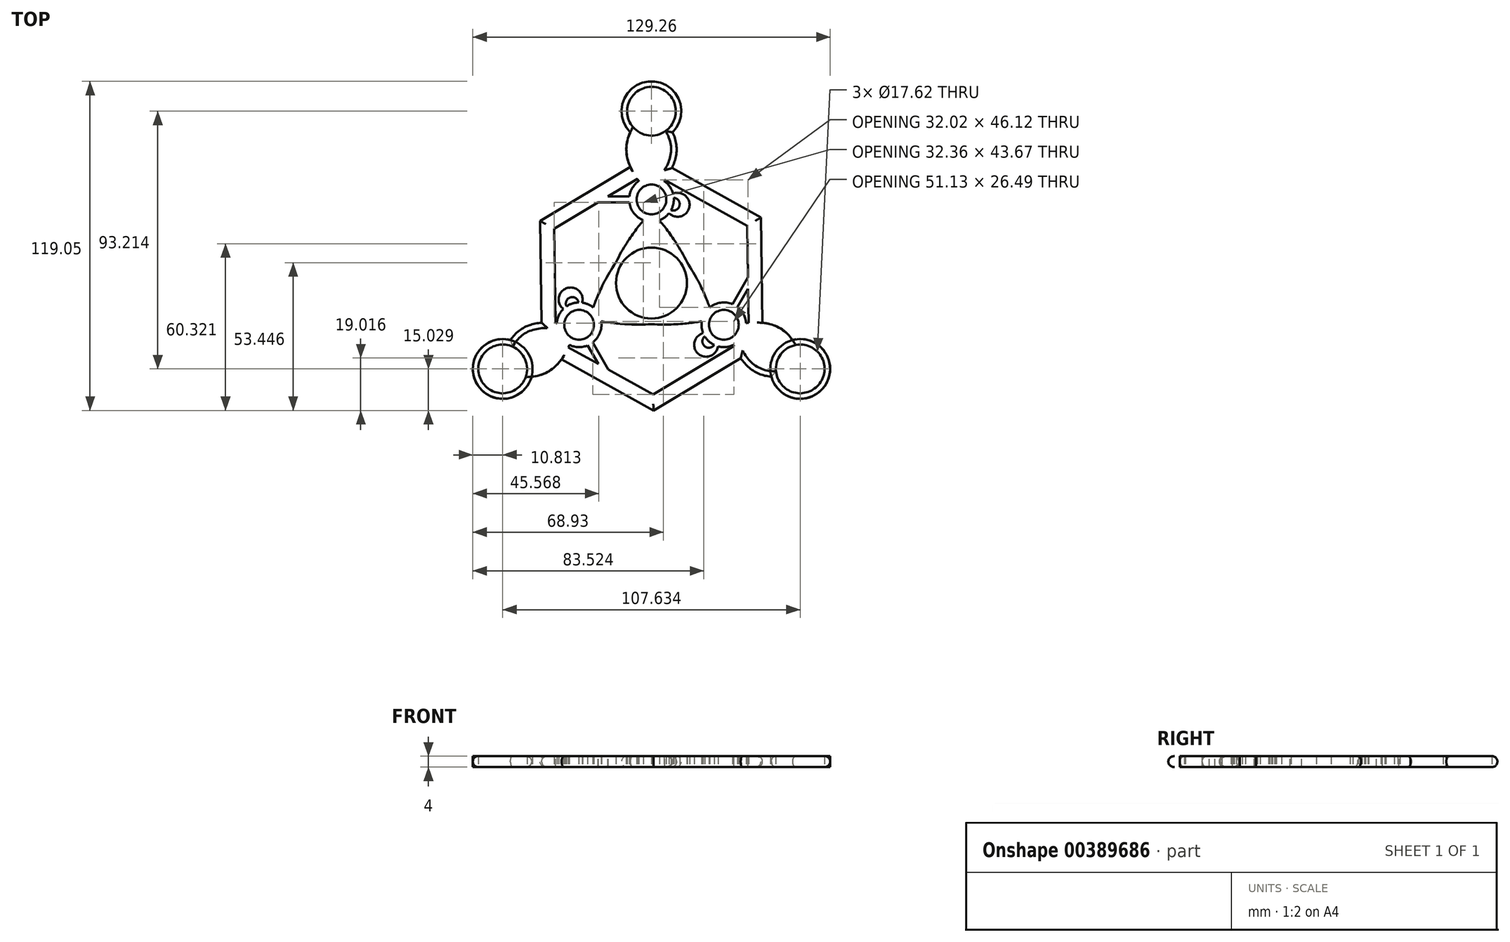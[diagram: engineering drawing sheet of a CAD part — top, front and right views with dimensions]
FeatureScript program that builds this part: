
annotation { "Feature Type Name" : "Feature", "Feature Type Description" : "" }
export const myFeature = defineFeature(function(context is Context, id is Id, definition is map)
    precondition{}
    {
        {
            var Q0;
            Q0=qCreatedBy(makeId("Top.planeOp"),FACE);
            var sketch = newSketch(context, id + "F0", { "sketchPlane" : qUnion([Q0])});
            skCircle(sketch, "E0", {"center": v(0, 0) * mm, "radius": 14.84 * mm});
            skCircle(sketch, "E1", {"center": v(0, 62.14) * mm, "radius": 10.8 * mm});
            skFitSpline(sketch, "E2", {"points": [v(-13.39, 6.4) * mm, v(0, 30.23) * mm, v(-7.64, 54.5) * mm], "startDerivative": vector(48.16, 100) * mm, "endDerivative": vector(32.63, 68.5) * mm});
            skFitSpline(sketch, "E3.MirrorCS", {"points": [v(13.39, 6.4) * mm, v(0, 30.23) * mm, v(7.64, 54.5) * mm], "startDerivative": vector(-48.16, 100) * mm, "endDerivative": vector(-32.63, 68.5) * mm});
            skCircle(sketch, "E4", {"center": v(0, 30.23) * mm, "radius": 5.38 * mm});
            skArc(sketch, "E5.0", {"start": v(-4.57, 36.9) * mm, "mid": v(-6.89, 34.45) * mm, "end": v(-8.01, 31.27) * mm});
            skFitSpline(sketch, "E6.trimOffspring", {"points": [v(-13.39, 6.4) * mm, v(0, 30.23) * mm, v(-7.64, 54.5) * mm], "startDerivative": vector(48.16, 100) * mm, "endDerivative": vector(32.63, 68.5) * mm});
            skLineSegment(sketch, "E7.trimOffspring", {"start": v(0, 30.23) * mm, "end": v(0, 30.23) * mm});
            skArc(sketch, "E8.trimOffspring", {"start": v(2.88, 22.68) * mm, "mid": v(6.82, 25.9) * mm, "end": v(8.06, 30.83) * mm});
            skCircle(sketch, "E9.1.0", {"center": v(-53.82, -31.07) * mm, "radius": 10.8 * mm});
            skCircle(sketch, "E9.2.0", {"center": v(53.82, -31.07) * mm, "radius": 10.8 * mm});
            skCircle(sketch, "E10.0", {"center": v(0, 0) * mm, "radius": 12.84 * mm});
            skCircle(sketch, "E11.0", {"center": v(0, 62.14) * mm, "radius": 8.8 * mm});
            skLineSegment(sketch, "E12.bottom", {"start": v(-20.22, 31.3) * mm, "end": v(-8.01, 31.3) * mm});
            skLineSegment(sketch, "E12.top", {"start": v(-20.22, 29.18) * mm, "end": v(-8.01, 29.18) * mm});
            skLineSegment(sketch, "E12.left", {"start": v(-20.22, 31.3) * mm, "end": v(-20.22, 29.18) * mm});
            skLineSegment(sketch, "E12.right", {"start": v(-8.01, 31.3) * mm, "end": v(-8.01, 31.27) * mm});
            skArc(sketch, "E13.trimOffspring", {"start": v(-8.01, 29.18) * mm, "mid": v(-6.34, 25.22) * mm, "end": v(-2.88, 22.68) * mm});
            skArc(sketch, "E14", {"start": v(7.08, 26.34) * mm, "mid": v(10.17, 28.03) * mm, "end": v(8.06, 30.83) * mm});
            skArc(sketch, "E15", {"start": v(5.35, 29.7) * mm, "mid": v(5.2, 29.16) * mm, "end": v(5.13, 28.62) * mm});
            skArc(sketch, "E16.trimOffspring", {"start": v(7.8, 32.3) * mm, "mid": v(6.6, 34.89) * mm, "end": v(4.57, 36.9) * mm});
            skArc(sketch, "E17.trimOffspring", {"start": v(6.37, 25.26) * mm, "mid": v(13.7, 27.43) * mm, "end": v(7.8, 32.3) * mm});
            skSolve(sketch);
        }
        {
            var Q0;
            Q0=qSketchRegion(id+"F0",true);
            extrude(context, id + "F1", {"entities" : qUnion([Q0]), "depth" : 4 * mm});
        }
        {
            var Q0;
            Q0=makeQuery(id+"F1.opExtrude","SWEPT_BODY",BODY,{"disambiguationData":[OSD([sQuery(id+"F0.wireOp",EDGE,"E0"),sQuery(id+"F0.wireOp",EDGE,"E1"),sQuery(id+"F0.wireOp",EDGE,"E2"),sQuery(id+"F0.wireOp",EDGE,"E3.MirrorCS"),sQuery(id+"F0.wireOp",EDGE,"E4"),sQuery(id+"F0.wireOp",EDGE,"E5.0"),sQuery(id+"F0.wireOp",EDGE,"E3.MirrorCS"),sQuery(id+"F0.wireOp",EDGE,"E6.trimOffspring"),sQuery(id+"F0.wireOp",EDGE,"E8.trimOffspring"),sQuery(id+"F0.wireOp",EDGE,"E10.0"),sQuery(id+"F0.wireOp",EDGE,"E11.0")])]});
            var Q1;
            Q1=makeQuery(id+"F1.opExtrude","CAP_EDGE",EDGE,{"disambiguationData":[OSD([sQuery(id+"F0.wireOp",EDGE,"E10.0")])],"isStart":false});
            circularPattern(context, id + "F2", {"entities" : qUnion([Q0]), "axis" : qUnion([Q1]), "angle" : 360 * degree, "instanceCount" : 3, "equalSpace" : true});
        }
        {
            var Q0;
            Q0=qCreatedBy(makeId("Top.planeOp"),FACE);
            var sketch = newSketch(context, id + "F3", { "sketchPlane" : qUnion([Q0])});
            skCircle(sketch, "E18.cCircle", {"center": v(0, 0) * mm, "radius": 39.93 * mm, "construction": true});
            skLineSegment(sketch, "E18.0", {"start": v(0.71, -46.1) * mm, "end": v(-39.57, -23.67) * mm});
            skLineSegment(sketch, "E18.1", {"start": v(-39.57, -23.67) * mm, "end": v(-40.28, 22.43) * mm});
            skLineSegment(sketch, "E18.2", {"start": v(-40.28, 22.43) * mm, "end": v(-0.71, 46.1) * mm});
            skLineSegment(sketch, "E18.3", {"start": v(-0.71, 46.1) * mm, "end": v(39.57, 23.67) * mm});
            skLineSegment(sketch, "E18.4", {"start": v(39.57, 23.67) * mm, "end": v(40.28, -22.43) * mm});
            skLineSegment(sketch, "E18.5", {"start": v(40.28, -22.43) * mm, "end": v(0.71, -46.1) * mm});
            skPoint(sketch, "E18.0.midPoint", {"position": v(-19.43, -34.89) * mm});
            skLineSegment(sketch, "E19.0", {"start": v(-0.63, 40.33) * mm, "end": v(34.61, 20.7) * mm});
            skLineSegment(sketch, "E19.1", {"start": v(35.24, -19.62) * mm, "end": v(0.63, -40.33) * mm});
            skLineSegment(sketch, "E19.2", {"start": v(0.63, -40.33) * mm, "end": v(-34.61, -20.7) * mm});
            skLineSegment(sketch, "E19.3", {"start": v(34.61, 20.7) * mm, "end": v(35.24, -19.62) * mm});
            skLineSegment(sketch, "E19.4", {"start": v(-34.61, -20.7) * mm, "end": v(-35.24, 19.62) * mm});
            skLineSegment(sketch, "E19.5", {"start": v(-35.24, 19.62) * mm, "end": v(-0.63, 40.33) * mm});
            skSolve(sketch);
        }
        {
            var Q0;
            Q0=makeQuery(id+"F3.imprint","IMPRINT",FACE,{"disambiguationData":[TD([[makeQuery(id+"F3.imprint","IMPRINT",EDGE,{"derivedFrom":sQuery(id+"F3.wireOp",EDGE,"E18.0")}),-1.0]])]});
            extrude(context, id + "F4", {"entities" : qUnion([Q0]), "operationType" : NewBodyOperationType.ADD, "depth" : 4 * mm});
        }
        {
            var Q0;
            Q0=makeQuery(id+"F4.opExtrude","CAP_EDGE",EDGE,{"disambiguationData":[OSD([sQuery(id+"F3.wireOp",EDGE,"E18.3")])],"isStart":false});
            var Q1;
            Q1=makeQuery(id+"F4.opExtrude","CAP_EDGE",EDGE,{"disambiguationData":[OSD([sQuery(id+"F3.wireOp",EDGE,"E18.4")])],"isStart":false});
            var Q2;
            {var subQ0=sQuery(id+"F0.wireOp",EDGE,"E1");var subQ2=sQuery(id+"F0.wireOp",EDGE,"E6.trimOffspring");Q2=makeQuery(id+"F4.boolean.opBoolean","SPLIT",EDGE,{"disambiguationData":[TD([makeQuery(id+"F2.opPattern","COPY",FACE,{"derivedFrom":makeQuery(id+"F1.opExtrude","SWEPT_FACE",FACE,{"disambiguationData":[OSD([subQ0])]}),"instanceName":"2"})])],"derivedFrom":makeQuery(id+"F2.opPattern","COPY",EDGE,{"derivedFrom":makeQuery(id+"F1.opExtrude","CAP_EDGE",EDGE,{"disambiguationData":[OSD([subQ2])],"isStart":false}),"instanceName":"2"})});}
            var Q3;
            {var subQ0=sQuery(id+"F0.wireOp",EDGE,"E1");var subQ2=sQuery(id+"F0.wireOp",EDGE,"E3.MirrorCS");Q3=makeQuery(id+"F4.boolean.opBoolean","SPLIT",EDGE,{"disambiguationData":[TD([makeQuery(id+"F2.opPattern","COPY",FACE,{"derivedFrom":makeQuery(id+"F1.opExtrude","SWEPT_FACE",FACE,{"disambiguationData":[OSD([subQ0])]}),"instanceName":"2"})])],"derivedFrom":makeQuery(id+"F2.opPattern","COPY",EDGE,{"derivedFrom":makeQuery(id+"F1.opExtrude","CAP_EDGE",EDGE,{"disambiguationData":[OSD([subQ2])],"isStart":false}),"instanceName":"2"})});}
            var Q4;
            Q4=makeQuery(id+"F4.opExtrude","CAP_EDGE",EDGE,{"disambiguationData":[OSD([sQuery(id+"F3.wireOp",EDGE,"E18.5")])],"isStart":false});
            var Q5;
            Q5=makeQuery(id+"F4.opExtrude","CAP_EDGE",EDGE,{"disambiguationData":[OSD([sQuery(id+"F3.wireOp",EDGE,"E18.0")])],"isStart":false});
            var Q6;
            {var subQ0=sQuery(id+"F0.wireOp",EDGE,"E6.trimOffspring");var subQ1=sQuery(id+"F0.wireOp",EDGE,"E1");Q6=makeQuery(id+"F4.boolean.opBoolean","SPLIT",EDGE,{"disambiguationData":[TD([makeQuery(id+"F2.opPattern","COPY",FACE,{"derivedFrom":makeQuery(id+"F1.opExtrude","SWEPT_FACE",FACE,{"disambiguationData":[OSD([subQ1])]}),"instanceName":"1"})])],"derivedFrom":makeQuery(id+"F2.opPattern","COPY",EDGE,{"derivedFrom":makeQuery(id+"F1.opExtrude","CAP_EDGE",EDGE,{"disambiguationData":[OSD([subQ0])],"isStart":false}),"instanceName":"1"})});}
            var Q7;
            {var subQ0=sQuery(id+"F0.wireOp",EDGE,"E3.MirrorCS");var subQ1=sQuery(id+"F0.wireOp",EDGE,"E1");Q7=makeQuery(id+"F4.boolean.opBoolean","SPLIT",EDGE,{"disambiguationData":[TD([makeQuery(id+"F2.opPattern","COPY",FACE,{"derivedFrom":makeQuery(id+"F1.opExtrude","SWEPT_FACE",FACE,{"disambiguationData":[OSD([subQ1])]}),"instanceName":"1"})])],"derivedFrom":makeQuery(id+"F2.opPattern","COPY",EDGE,{"derivedFrom":makeQuery(id+"F1.opExtrude","CAP_EDGE",EDGE,{"disambiguationData":[OSD([subQ0])],"isStart":false}),"instanceName":"1"})});}
            var Q8;
            Q8=makeQuery(id+"F2.opPattern","COPY",EDGE,{"derivedFrom":makeQuery(id+"F1.opExtrude","CAP_EDGE",EDGE,{"disambiguationData":[OSD([sQuery(id+"F0.wireOp",EDGE,"E1")])],"isStart":false}),"instanceName":"1"});
            var Q9;
            Q9=makeQuery(id+"F2.opPattern","COPY",EDGE,{"derivedFrom":makeQuery(id+"F1.opExtrude","CAP_EDGE",EDGE,{"disambiguationData":[OSD([sQuery(id+"F0.wireOp",EDGE,"E1")])],"isStart":true}),"instanceName":"1"});
            var Q10;
            Q10=makeQuery(id+"F4.opExtrude","CAP_EDGE",EDGE,{"disambiguationData":[OSD([sQuery(id+"F3.wireOp",EDGE,"E18.1")])],"isStart":false});
            var Q11;
            Q11=makeQuery(id+"F4.opExtrude","CAP_EDGE",EDGE,{"disambiguationData":[OSD([sQuery(id+"F3.wireOp",EDGE,"E18.2")])],"isStart":false});
            var Q12;
            {var subQ0=sQuery(id+"F0.wireOp",EDGE,"E6.trimOffspring");var subQ2=sQuery(id+"F0.wireOp",EDGE,"E1");Q12=makeQuery(id+"F4.boolean.opBoolean","SPLIT",EDGE,{"disambiguationData":[TD([makeQuery(id+"F1.opExtrude","SWEPT_FACE",FACE,{"disambiguationData":[OSD([subQ2])]})])],"derivedFrom":makeQuery(id+"F1.opExtrude","CAP_EDGE",EDGE,{"disambiguationData":[OSD([subQ0])],"isStart":false})});}
            var Q13;
            Q13=makeQuery(id+"F1.opExtrude","CAP_EDGE",EDGE,{"disambiguationData":[OSD([sQuery(id+"F0.wireOp",EDGE,"E1")])],"isStart":false});
            var Q14;
            {var subQ0=sQuery(id+"F0.wireOp",EDGE,"E3.MirrorCS");var subQ1=sQuery(id+"F0.wireOp",EDGE,"E1");Q14=makeQuery(id+"F4.boolean.opBoolean","SPLIT",EDGE,{"disambiguationData":[TD([makeQuery(id+"F1.opExtrude","SWEPT_FACE",FACE,{"disambiguationData":[OSD([subQ1])]})])],"derivedFrom":makeQuery(id+"F1.opExtrude","CAP_EDGE",EDGE,{"disambiguationData":[OSD([subQ0])],"isStart":false})});}
            var Q15;
            Q15=makeQuery(id+"F2.opPattern","COPY",EDGE,{"derivedFrom":makeQuery(id+"F1.opExtrude","CAP_EDGE",EDGE,{"disambiguationData":[OSD([sQuery(id+"F0.wireOp",EDGE,"E1")])],"isStart":false}),"instanceName":"2"});
            var Q16;
            Q16=makeQuery(id+"F4.opExtrude","CAP_EDGE",EDGE,{"disambiguationData":[OSD([sQuery(id+"F3.wireOp",EDGE,"E18.5")])],"isStart":true});
            var Q17;
            Q17=makeQuery(id+"F4.opExtrude","CAP_EDGE",EDGE,{"disambiguationData":[OSD([sQuery(id+"F3.wireOp",EDGE,"E18.0")])],"isStart":true});
            var Q18;
            {var subQ0=sQuery(id+"F0.wireOp",EDGE,"E3.MirrorCS");var subQ1=sQuery(id+"F0.wireOp",EDGE,"E1");Q18=makeQuery(id+"F4.boolean.opBoolean","SPLIT",EDGE,{"disambiguationData":[TD([makeQuery(id+"F2.opPattern","COPY",FACE,{"derivedFrom":makeQuery(id+"F1.opExtrude","SWEPT_FACE",FACE,{"disambiguationData":[OSD([subQ1])]}),"instanceName":"2"})])],"derivedFrom":makeQuery(id+"F2.opPattern","COPY",EDGE,{"derivedFrom":makeQuery(id+"F1.opExtrude","CAP_EDGE",EDGE,{"disambiguationData":[OSD([subQ0])],"isStart":true}),"instanceName":"2"})});}
            var Q19;
            Q19=makeQuery(id+"F2.opPattern","COPY",EDGE,{"derivedFrom":makeQuery(id+"F1.opExtrude","CAP_EDGE",EDGE,{"disambiguationData":[OSD([sQuery(id+"F0.wireOp",EDGE,"E1")])],"isStart":true}),"instanceName":"2"});
            var Q20;
            {var subQ0=sQuery(id+"F0.wireOp",EDGE,"E6.trimOffspring");var subQ1=sQuery(id+"F0.wireOp",EDGE,"E1");Q20=makeQuery(id+"F4.boolean.opBoolean","SPLIT",EDGE,{"disambiguationData":[TD([makeQuery(id+"F2.opPattern","COPY",FACE,{"derivedFrom":makeQuery(id+"F1.opExtrude","SWEPT_FACE",FACE,{"disambiguationData":[OSD([subQ1])]}),"instanceName":"2"})])],"derivedFrom":makeQuery(id+"F2.opPattern","COPY",EDGE,{"derivedFrom":makeQuery(id+"F1.opExtrude","CAP_EDGE",EDGE,{"disambiguationData":[OSD([subQ0])],"isStart":true}),"instanceName":"2"})});}
            var Q21;
            Q21=makeQuery(id+"F4.opExtrude","CAP_EDGE",EDGE,{"disambiguationData":[OSD([sQuery(id+"F3.wireOp",EDGE,"E18.4")])],"isStart":true});
            var Q22;
            Q22=makeQuery(id+"F4.opExtrude","CAP_EDGE",EDGE,{"disambiguationData":[OSD([sQuery(id+"F3.wireOp",EDGE,"E18.3")])],"isStart":true});
            var Q23;
            {var subQ0=sQuery(id+"F0.wireOp",EDGE,"E3.MirrorCS");var subQ1=sQuery(id+"F0.wireOp",EDGE,"E1");Q23=makeQuery(id+"F4.boolean.opBoolean","SPLIT",EDGE,{"disambiguationData":[TD([makeQuery(id+"F1.opExtrude","SWEPT_FACE",FACE,{"disambiguationData":[OSD([subQ1])]})])],"derivedFrom":makeQuery(id+"F1.opExtrude","CAP_EDGE",EDGE,{"disambiguationData":[OSD([subQ0])],"isStart":true})});}
            var Q24;
            Q24=makeQuery(id+"F1.opExtrude","CAP_EDGE",EDGE,{"disambiguationData":[OSD([sQuery(id+"F0.wireOp",EDGE,"E1")])],"isStart":true});
            var Q25;
            {var subQ0=sQuery(id+"F0.wireOp",EDGE,"E6.trimOffspring");var subQ1=sQuery(id+"F0.wireOp",EDGE,"E1");Q25=makeQuery(id+"F4.boolean.opBoolean","SPLIT",EDGE,{"disambiguationData":[TD([makeQuery(id+"F1.opExtrude","SWEPT_FACE",FACE,{"disambiguationData":[OSD([subQ1])]})])],"derivedFrom":makeQuery(id+"F1.opExtrude","CAP_EDGE",EDGE,{"disambiguationData":[OSD([subQ0])],"isStart":true})});}
            var Q26;
            Q26=makeQuery(id+"F4.opExtrude","CAP_EDGE",EDGE,{"disambiguationData":[OSD([sQuery(id+"F3.wireOp",EDGE,"E18.2")])],"isStart":true});
            var Q27;
            {var subQ0=sQuery(id+"F0.wireOp",EDGE,"E6.trimOffspring");var subQ1=sQuery(id+"F0.wireOp",EDGE,"E1");Q27=makeQuery(id+"F4.boolean.opBoolean","SPLIT",EDGE,{"disambiguationData":[TD([makeQuery(id+"F2.opPattern","COPY",FACE,{"derivedFrom":makeQuery(id+"F1.opExtrude","SWEPT_FACE",FACE,{"disambiguationData":[OSD([subQ1])]}),"instanceName":"1"})])],"derivedFrom":makeQuery(id+"F2.opPattern","COPY",EDGE,{"derivedFrom":makeQuery(id+"F1.opExtrude","CAP_EDGE",EDGE,{"disambiguationData":[OSD([subQ0])],"isStart":true}),"instanceName":"1"})});}
            var Q28;
            {var subQ0=sQuery(id+"F0.wireOp",EDGE,"E3.MirrorCS");var subQ1=sQuery(id+"F0.wireOp",EDGE,"E1");Q28=makeQuery(id+"F4.boolean.opBoolean","SPLIT",EDGE,{"disambiguationData":[TD([makeQuery(id+"F2.opPattern","COPY",FACE,{"derivedFrom":makeQuery(id+"F1.opExtrude","SWEPT_FACE",FACE,{"disambiguationData":[OSD([subQ1])]}),"instanceName":"1"})])],"derivedFrom":makeQuery(id+"F2.opPattern","COPY",EDGE,{"derivedFrom":makeQuery(id+"F1.opExtrude","CAP_EDGE",EDGE,{"disambiguationData":[OSD([subQ0])],"isStart":true}),"instanceName":"1"})});}
            var Q29;
            Q29=makeQuery(id+"F4.opExtrude","CAP_EDGE",EDGE,{"disambiguationData":[OSD([sQuery(id+"F3.wireOp",EDGE,"E18.1")])],"isStart":true});
            fillet(context, id + "F5", {"entities" : qUnion([Q0, Q1, Q2, Q3, Q4, Q5, Q6, Q7, Q8, Q9, Q10, Q11, Q12, Q13, Q14, Q15, Q16, Q17, Q18, Q19, Q20, Q21, Q22, Q23, Q24, Q25, Q26, Q27, Q28, Q29]), "radius" : 2 * mm, "tangentPropagation" : true, "allowEdgeOverflow" : false});
        }
    });
